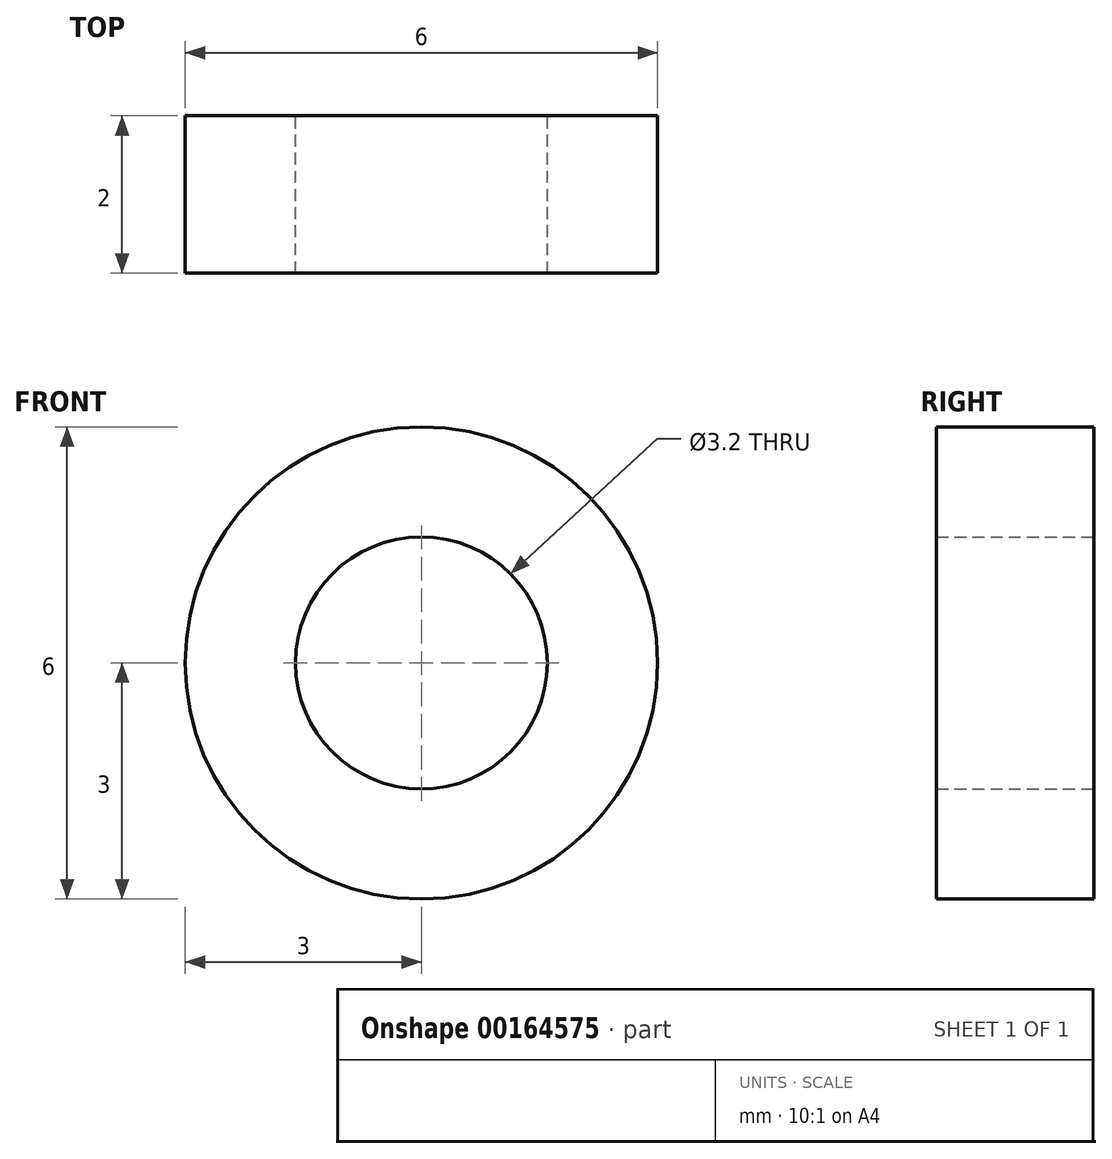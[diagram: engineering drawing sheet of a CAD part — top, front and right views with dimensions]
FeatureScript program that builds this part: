
annotation { "Feature Type Name" : "Feature", "Feature Type Description" : "" }
export const myFeature = defineFeature(function(context is Context, id is Id, definition is map)
    precondition{}
    {
        {
            var Q0;
            Q0=qCreatedBy(makeId("Front.planeOp"),FACE);
            var sketch = newSketch(context, id + "F0", { "sketchPlane" : qUnion([Q0])});
            skCircle(sketch, "E0", {"center": v(0, 0) * mm, "radius": 1.6 * mm});
            skCircle(sketch, "E1", {"center": v(0, 0) * mm, "radius": 3 * mm});
            skSolve(sketch);
        }
        {
            var Q0;
            Q0 = qSketchRegion(id + "F0", true);
            extrude(context, id + "F1", {"entities" : qUnion([Q0]), "depth" : 2 * mm});
        }
    });
